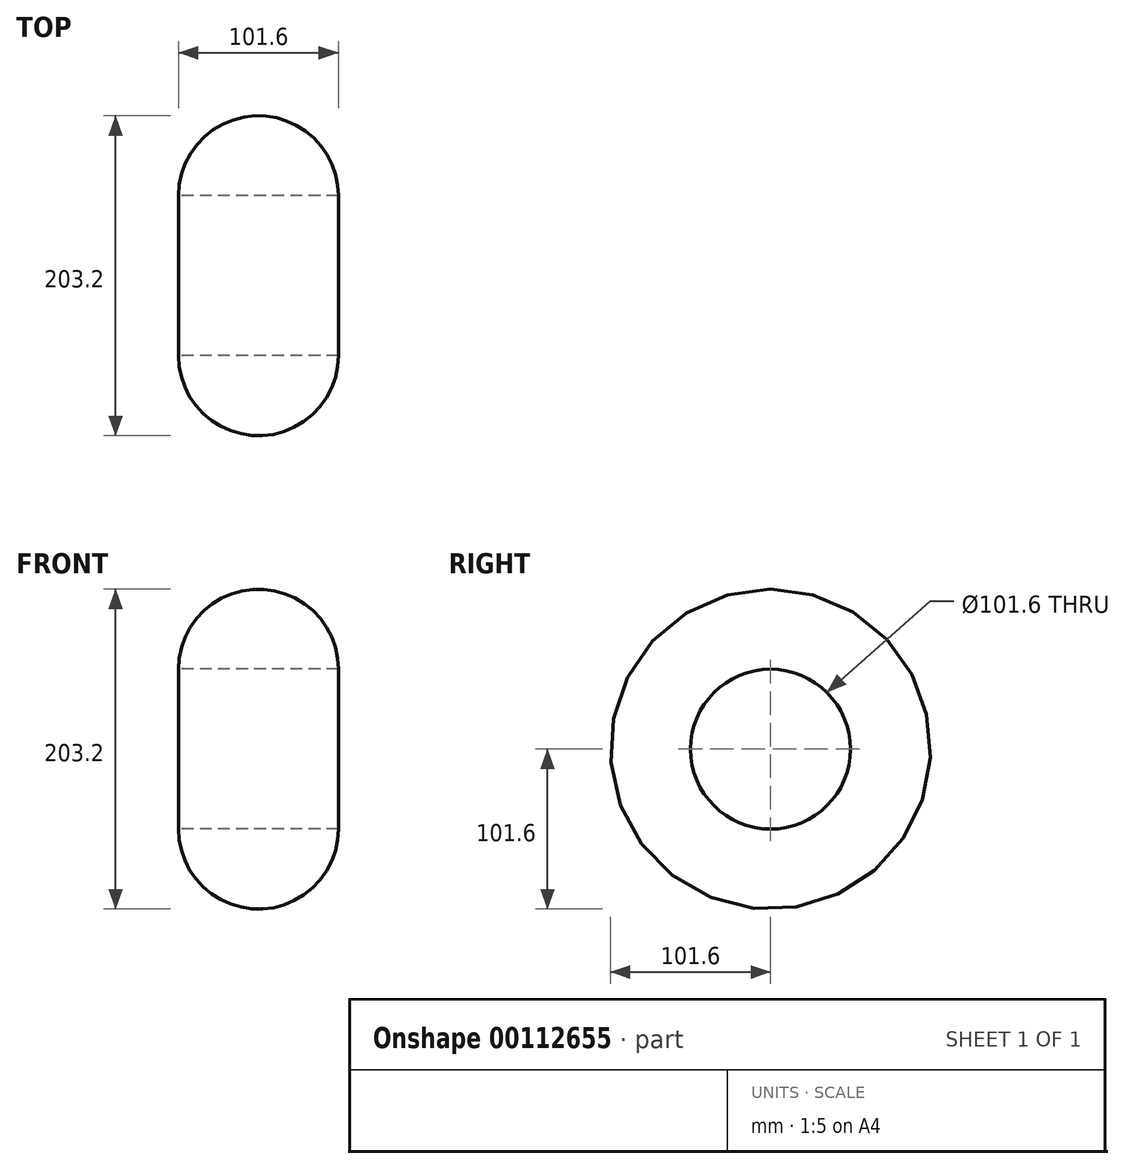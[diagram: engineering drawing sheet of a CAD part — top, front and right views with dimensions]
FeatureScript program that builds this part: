
annotation { "Feature Type Name" : "Feature", "Feature Type Description" : "" }
export const myFeature = defineFeature(function(context is Context, id is Id, definition is map)
    precondition{}
    {
        {
            var Q0;
            Q0=qCreatedBy(makeId("Top.planeOp"),FACE);
            var sketch = newSketch(context, id + "F0", { "sketchPlane" : qUnion([Q0])});
            skLineSegment(sketch, "E0.bottom", {"start": v(0, 0) * mm, "end": v(101.6, 0) * mm, "construction": true});
            skLineSegment(sketch, "E0.top", {"start": v(0, 50.8) * mm, "end": v(101.6, 50.8) * mm});
            skLineSegment(sketch, "E0.left", {"start": v(0, 0) * mm, "end": v(0, 50.8) * mm, "construction": true});
            skLineSegment(sketch, "E0.right", {"start": v(101.6, 0) * mm, "end": v(101.6, 50.8) * mm, "construction": true});
            skArc(sketch, "E1", {"start": v(101.6, 50.8) * mm, "mid": v(50.8, 101.6) * mm, "end": v(0, 50.8) * mm});
            skSolve(sketch);
        }
        {
            var Q0;
            Q0=qCreatedBy(makeId("Right.planeOp"),FACE);
            var sketch = newSketch(context, id + "F1", { "sketchPlane" : qUnion([Q0])});
            skCircle(sketch, "E2", {"center": v(0, 0) * mm, "radius": 12.7 * mm});
            skSolve(sketch);
        }
        {
            var Q0;
            Q0=makeQuery(id+"F0.imprint","IMPRINT",FACE,{"disambiguationData":[TD([[makeQuery(id+"F0.imprint","IMPRINT",EDGE,{"derivedFrom":sQuery(id+"F0.wireOp",EDGE,"E0.top")}),1.0]])]});
            var Q1;
            Q1=sQuery(id+"F1.wireOp",EDGE,"E2");
            revolve(context, id + "F2", {"entities" : qUnion([Q0]), "axis" : qUnion([Q1]), "revolveType" : RevolveType.FULL});
        }
    });
